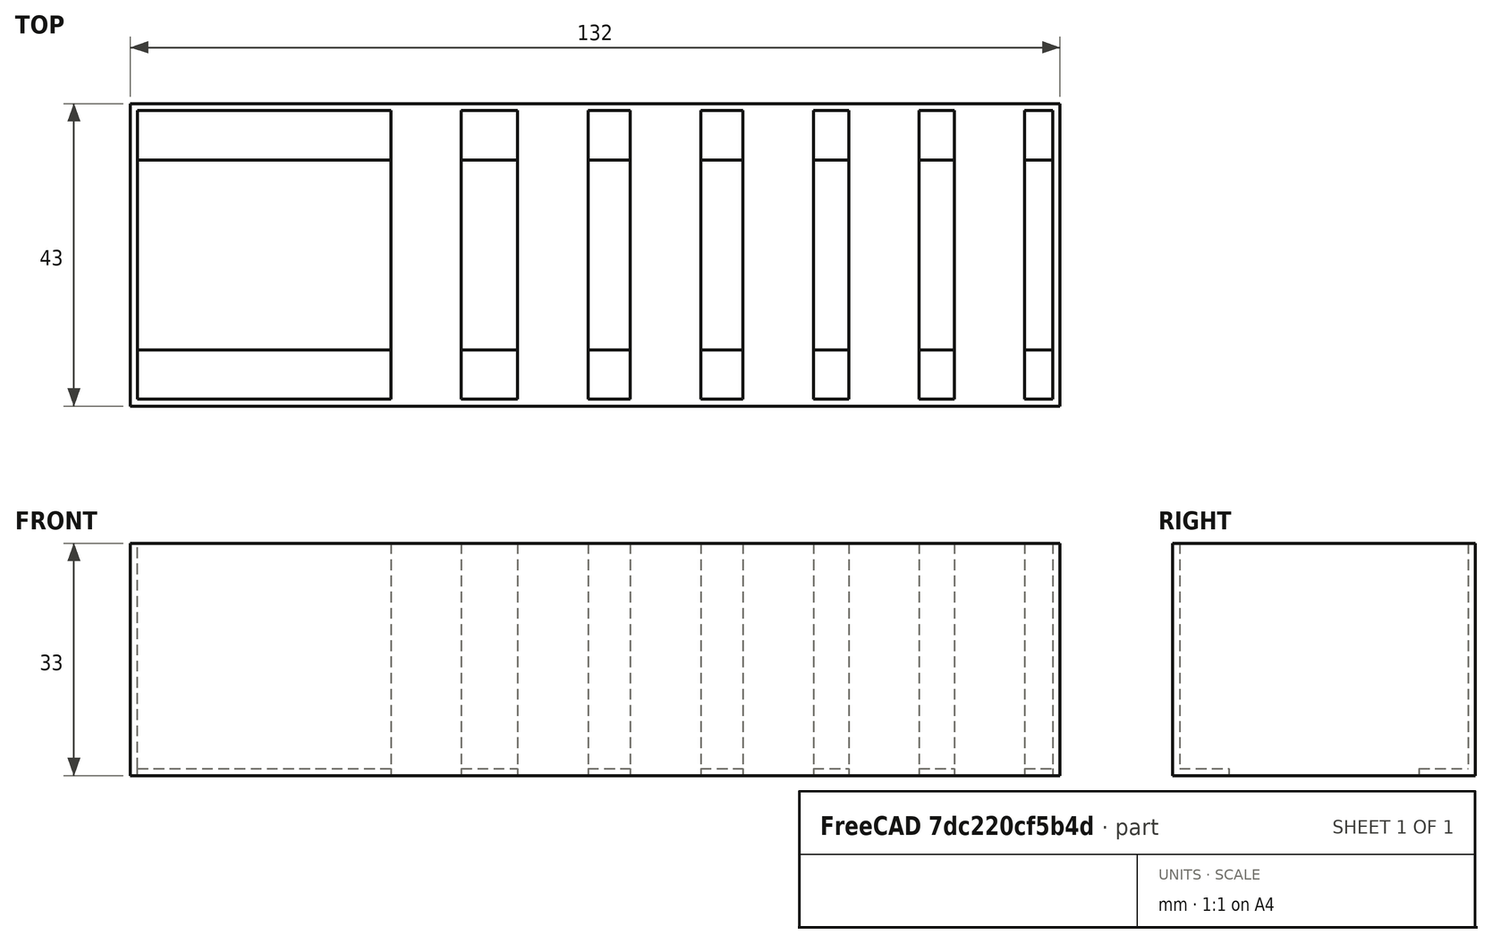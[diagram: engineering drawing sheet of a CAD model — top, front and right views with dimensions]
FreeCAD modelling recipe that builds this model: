
FCSTD DOCUMENT  (FreeCAD 0.18R4 (GitTag))
Label: city
License: All rights reserved
LicenseURL: http://en.wikipedia.org/wiki/All_rights_reserved
objects: Part::Box×12, Part::Cut×2, Part::MultiFuse×2
note: 16 computed .brp shape members not serialized (recipe doc carries the construction recipe); baked Part::Feature solids carry a one-line shape summary decoded from their .brp

FEATURE [Part::Box] Box  label="Cube"
  AttacherType = Attacher::AttachEngine3D
  Height = 33
  Length = 202
  Width = 43
FEATURE [Part::Box] Box001  label="Cube001"
  AttacherType = Attacher::AttachEngine3D
  Height = 33
  Length = 200
  Placement = pos=(1,1,0) rot=(0,0,1;0rad)
  Width = 41
FEATURE [Part::Cut] Cut
  Base = -> Box
  Tool = -> Box001
FEATURE [Part::Box] Box002  label="Cube002"
  AttacherType = Attacher::AttachEngine3D
  Height = 1
  Length = 202
  Width = 8
FEATURE [Part::Box] Box003  label="Cube003"
  AttacherType = Attacher::AttachEngine3D
  Height = 1
  Length = 202
  Placement = pos=(0,35,0) rot=(0,0,1;0rad)
  Width = 8
FEATURE [Part::MultiFuse] Fusion
  Shapes = -> [Cut,Box002,Box003]
FEATURE [Part::Box] Box004  label="Cube004"
  AttacherType = Attacher::AttachEngine3D
  Height = 33
  Length = 10
  Placement = pos=(37,0,0) rot=(0,0,1;0rad)
  Width = 43
FEATURE [Part::Box] Box005  label="Cube005"
  AttacherType = Attacher::AttachEngine3D
  Height = 33
  Length = 10
  Placement = pos=(55,0,0) rot=(0,0,1;0rad)
  Width = 43
FEATURE [Part::Box] Box006  label="Cube006"
  AttacherType = Attacher::AttachEngine3D
  Height = 33
  Length = 10
  Placement = pos=(71,0,0) rot=(0,0,1;0rad)
  Width = 43
FEATURE [Part::Box] Box007  label="Cube007"
  AttacherType = Attacher::AttachEngine3D
  Height = 33
  Length = 10
  Placement = pos=(87,0,0) rot=(0,0,1;0rad)
  Width = 43
FEATURE [Part::Box] Box008  label="Cube008"
  AttacherType = Attacher::AttachEngine3D
  Height = 33
  Length = 10
  Placement = pos=(102,0,0) rot=(0,0,1;0rad)
  Width = 43
FEATURE [Part::Box] Box009  label="Cube009"
  AttacherType = Attacher::AttachEngine3D
  Height = 33
  Length = 10
  Placement = pos=(117,0,0) rot=(0,0,1;0rad)
  Width = 43
FEATURE [Part::Box] Box010  label="Cube010"
  AttacherType = Attacher::AttachEngine3D
  Height = 33
  Length = 10
  Placement = pos=(131,0,0) rot=(0,0,1;0rad)
  Width = 43
FEATURE [Part::Box] Box011  label="Cube011"
  AttacherType = Attacher::AttachEngine3D
  Height = 33
  Length = 70
  Placement = pos=(132,0,0) rot=(0,0,1;0rad)
  Width = 43
FEATURE [Part::MultiFuse] Fusion001
  Shapes = -> [Fusion,Box005,Box006,Box009,Box008,Box007,Box010,Box004]
FEATURE [Part::Cut] Cut001
  Base = -> Fusion001
  Tool = -> Box011
